# Revit family: Pressure_Reducing_Valve-Zurn_Wilkins-Model_NR3XLDUCPEX-(12-1_Inch)
name_source: partatom
category: Pipe Accessories
units: mm (PartAtom-declared; Revit-internal decimal feet)

## family parameters
Always vertical = Yes
Cut with Voids When Loaded = No
OmniClass Number = 23.65.55.14.17
OmniClass Title = Adjusting/Controlling Valves for Liquid Services
Part Type = Valve - Breaks Into
Round Connector Dimension = Use Radius
Shared = No
Work Plane-Based = No

## types (3) — shared parameters
Assembly Code = D2020300
Bell Base Length = 0' - 0 3/16"
Bell Base Radius = 0' - 1 1/32"
Bell Blend Radius = 0' - 0 3/4"
Bell Hex Radius = 0' - 0 13/16"
Bell Upper Base Length = 0' - 1 3/16"
Bell Upper Base Radius = 0' - 0 7/8"
Body Top Length = 0' - 1 5/32"
Body Top Seat Bell Radius = 0' - 1 1/4"
DIM B - Overall Height = 0' - 6 1/4"
DIM C - Body Center to Tail Length = 0' - 1 1/8"
DIM D - Bell base diameter = 0' - 2 1/2"
Default Elevation = 0' - 0"
Description = Water Pressure Reducing Valve with Integral By-pass check Valve and Strainer
Factory Preset Pressure = 50.00 psi
Flow Rate (GPM) = 0 GPM
MR copper sweat dia = 0' - 1"
Main Material = Paint - Zurn - Bronze
Manufacturer = Zurn Water, LLC
Manufacturer Brand = Zurn Wilkins
Max Working Water Pressure = 400.00 psi
Max Working Water Temperature = 140 °F
Model = NR3XLDUCPEX
Modified Date = 08/22/2025
Product Documentation Link = https://files.zurn.com
Product Installation Sheet URL = https://files.zurn.com
Product Page URL = https://www.zurn.com
Product data URL = https://www.bimobject.com
Reduced Pressure Range = 15 to 75 psi
Repair Parts URL = https://files.zurn.com
Width = 0' - 0"
bottom of pex barb fitting = 0' - 0 9/32"
pex length = 0' - 1"
top of pex barb fitting = 0' - 0 11/32"

## per-type parameters (varying)
- 1-NR3XLDUCPEX (1" NR3XLDUCPEX): Body Base Tail Radius=0' - 0 13/16"; Body Radius=0' - 0 27/32"; Body Seat Bell Length=0' - 0 15/32"; Body Tail Radius=0' - 0 7/16"; Body Thread Radius=0' - 0 7/8"; Body Top Radius=0' - 1"; Body Width=0' - 0 17/32"; Center to pex tailpiece end=0' - 3 5/32"; DIM A - LESS UNION (Main body length)=0' - 4"; Dimension A=0' - 4 15/16"; Horizontal pex alignment=0' - 0 3/4"; MR End to hex=0' - 0 7/8"; MR hex nut thickness=0' - 0 21/32"; MR hex nut width=0' - 2"; MR left end to hex nut=0' - 0 11/16"; MR pex pipe dia=0' - 1"; Nominal Diameter=0' - 1"; Nominal Radius=0' - 0 1/2"; Nut Length=0' - 2 1/4"; Nut Size=Nut : 1 inch; Overall length of the valve=0' - 6 1/8"; Polygon diameter=0' - 2 1/4"; Product Weight (lbs)=5; Tailpiece radius=0' - 0 3/4"; URL=http://www.zurn.com; pex fitting=pex fitting : 1 inch pex fitting
- 34-NR3XLDUCPEX (3/4" NR3XLDUCPEX): Body Base Tail Radius=0' - 0 5/8"; Body Radius=0' - 0 11/16"; Body Seat Bell Length=0' - 0 1/2"; Body Tail Radius=0' - 0 11/32"; Body Thread Radius=0' - 0 13/16"; Body Top Radius=0' - 1 1/16"; Body Width=0' - 0 3/8"; Center to pex tailpiece end=0' - 2 29/32"; DIM A - LESS UNION (Main body length)=0' - 3 1/2"; Dimension A=0' - 4 7/16"; Horizontal pex alignment=0' - 0 21/32"; MR End to hex=0' - 0 25/32"; MR hex nut thickness=0' - 0 5/8"; MR hex nut width=0' - 1 3/4"; MR left end to hex nut=0' - 0 19/32"; MR pex pipe dia=0' - 0 3/4"; Nominal Diameter=0' - 0 3/4"; Nominal Radius=0' - 0 3/8"; Nut Length=0' - 2 1/8"; Nut Size=Nut : 3/4 inch; Overall length of the valve=0' - 5 5/8"; Polygon diameter=0' - 2 1/4"; Product Weight (lbs)=3; Tailpiece radius=0' - 0 5/8"; URL=http://www.zurn.com; pex fitting=pex fitting : 3/4 inch pex fitting
- 12-NR3XLDUCPEX (1/2" NR3XLDUCPEX): Body Base Tail Radius=0' - 0 5/8"; Body Radius=0' - 0 11/16"; Body Seat Bell Length=0' - 0 15/32"; Body Tail Radius=0' - 0 7/16"; Body Thread Radius=0' - 0 13/16"; Body Top Radius=0' - 1 1/16"; Body Width=0' - 0 7/16"; Center to pex tailpiece end=0' - 2 29/32"; DIM A - LESS UNION (Main body length)=0' - 3 1/2"; Dimension A=0' - 4 3/8"; Horizontal pex alignment=0' - 0 9/16"; MR End to hex=0' - 0 7/8"; MR hex nut thickness=0' - 0 5/8"; MR hex nut width=0' - 1 3/4"; MR left end to hex nut=0' - 0 11/16"; MR pex pipe dia=0' - 0 1/2"; Nominal Diameter=0' - 0 1/2"; Nominal Radius=0' - 0 1/4"; Nut Length=0' - 2 1/16"; Nut Size=Nut : 1/2 inch; Overall length of the valve=0' - 5 5/8"; Polygon diameter=0' - 1 3/4"; Product Weight (lbs)=3; Tailpiece radius=0' - 0 1/2"; URL=https://www.zurn.com; pex fitting=pex fitting : 1/2 inch pex fitting

## geometry (parser evidence)
native form markers: Blend x1, Sweep x12
no freeform markers — native parametric forms only
